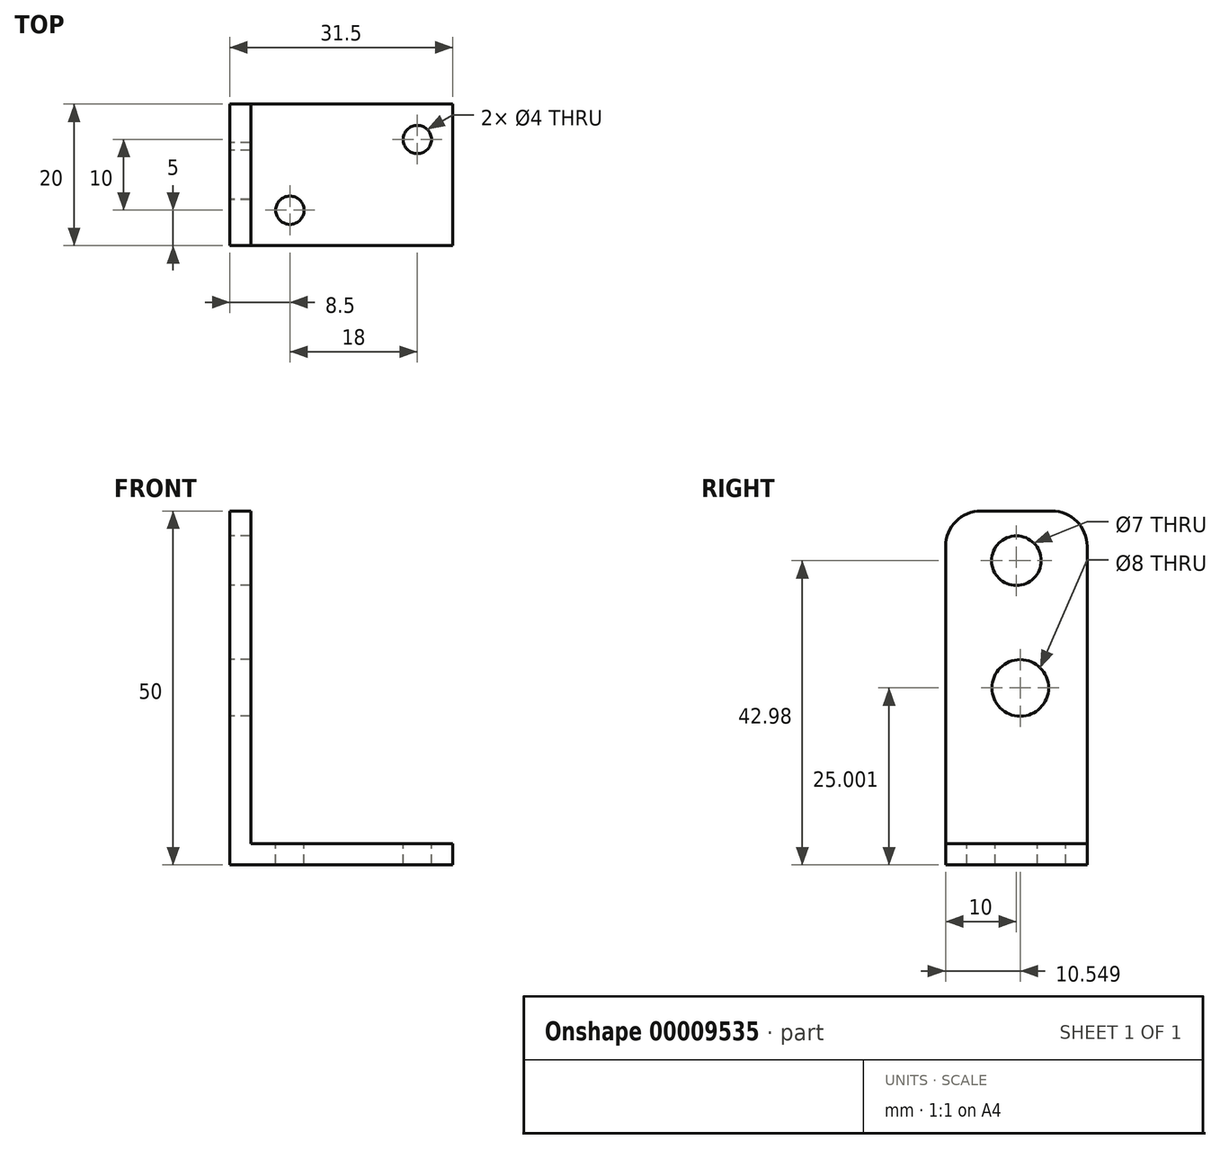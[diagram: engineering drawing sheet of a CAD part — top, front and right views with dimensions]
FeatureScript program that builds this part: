
annotation { "Feature Type Name" : "Feature", "Feature Type Description" : "" }
export const myFeature = defineFeature(function(context is Context, id is Id, definition is map)
    precondition{}
    {
        {
            var Q0;
            Q0=qCreatedBy(makeId("Right.planeOp"),FACE);
            var sketch = newSketch(context, id + "F0", { "sketchPlane" : qUnion([Q0])});
            skCircle(sketch, "E0", {"center": v(0, 0) * mm, "radius": 3.5 * mm});
            skLineSegment(sketch, "E1", {"start": v(-10, -42.98) * mm, "end": v(10, -42.98) * mm});
            skLineSegment(sketch, "E2", {"start": v(0, 12.72) * mm, "end": v(0, -46.69) * mm, "construction": true});
            skLineSegment(sketch, "E3", {"start": v(-10, 2.02) * mm, "end": v(-10, -42.98) * mm});
            skLineSegment(sketch, "E4", {"start": v(-5, 7.02) * mm, "end": v(5, 7.02) * mm});
            skLineSegment(sketch, "E5", {"start": v(10, 2.02) * mm, "end": v(10, -42.98) * mm});
            skCircle(sketch, "E6", {"center": v(0.55, -17.98) * mm, "radius": 4 * mm});
            skPoint(sketch, "E7.visualSharp", {"position": v(-10, 7.02) * mm});
            skArc(sketch, "E7.filletArc", {"start": v(-5, 7.02) * mm, "mid": v(-8.54, 5.56) * mm, "end": v(-10, 2.02) * mm});
            skPoint(sketch, "E8.visualSharp", {"position": v(10, 7.02) * mm});
            skArc(sketch, "E8.filletArc", {"start": v(10, 2.02) * mm, "mid": v(8.54, 5.56) * mm, "end": v(5, 7.02) * mm});
            skLineSegment(sketch, "E9", {"start": v(-10, -39.98) * mm, "end": v(10, -39.98) * mm});
            skSolve(sketch);
        }
        {
            var Q0;
            {var subQ2=sQuery(id+"F0.wireOp",EDGE,"E1");Q0=makeQuery(id+"F0.imprint","IMPRINT",FACE,{"disambiguationData":[TD([[makeQuery(id+"F0.imprint","IMPRINT",EDGE,{"derivedFrom":subQ2}),1.0]])]});}
            extrude(context, id + "F1", {"entities" : qUnion([Q0]), "depth" : 31.5 * mm});
        }
        {
            var Q0;
            Q0 = qSketchRegion(id + "F0", true);
            extrude(context, id + "F2", {"entities" : qUnion([Q0]), "operationType" : NewBodyOperationType.ADD, "depth" : 3 * mm});
        }
        {
            var Q0;
            Q0=qCreatedBy(makeId("Top.planeOp"),FACE);
            var sketch = newSketch(context, id + "F3", { "sketchPlane" : qUnion([Q0])});
            skCircle(sketch, "E10", {"center": v(26.5, 5) * mm, "radius": 2 * mm});
            skCircle(sketch, "E11", {"center": v(8.5, -5) * mm, "radius": 2 * mm});
            skSolve(sketch);
        }
        {
            var Q0;
            Q0=makeQuery(id+"F3.imprint","IMPRINT",FACE,{"disambiguationData":[TD([[makeQuery(id+"F3.imprint","IMPRINT",EDGE,{"derivedFrom":sQuery(id+"F3.wireOp",EDGE,"E10")}),1.0]])]});
            var Q1;
            Q1=makeQuery(id+"F3.imprint","IMPRINT",FACE,{"disambiguationData":[TD([[makeQuery(id+"F3.imprint","IMPRINT",EDGE,{"derivedFrom":sQuery(id+"F3.wireOp",EDGE,"E11")}),1.0]])]});
            extrude(context, id + "F4", {"entities" : qUnion([Q0, Q1]), "operationType" : NewBodyOperationType.REMOVE, "oppositeDirection" : true, "depth" : 55.92 * mm});
        }
    });
